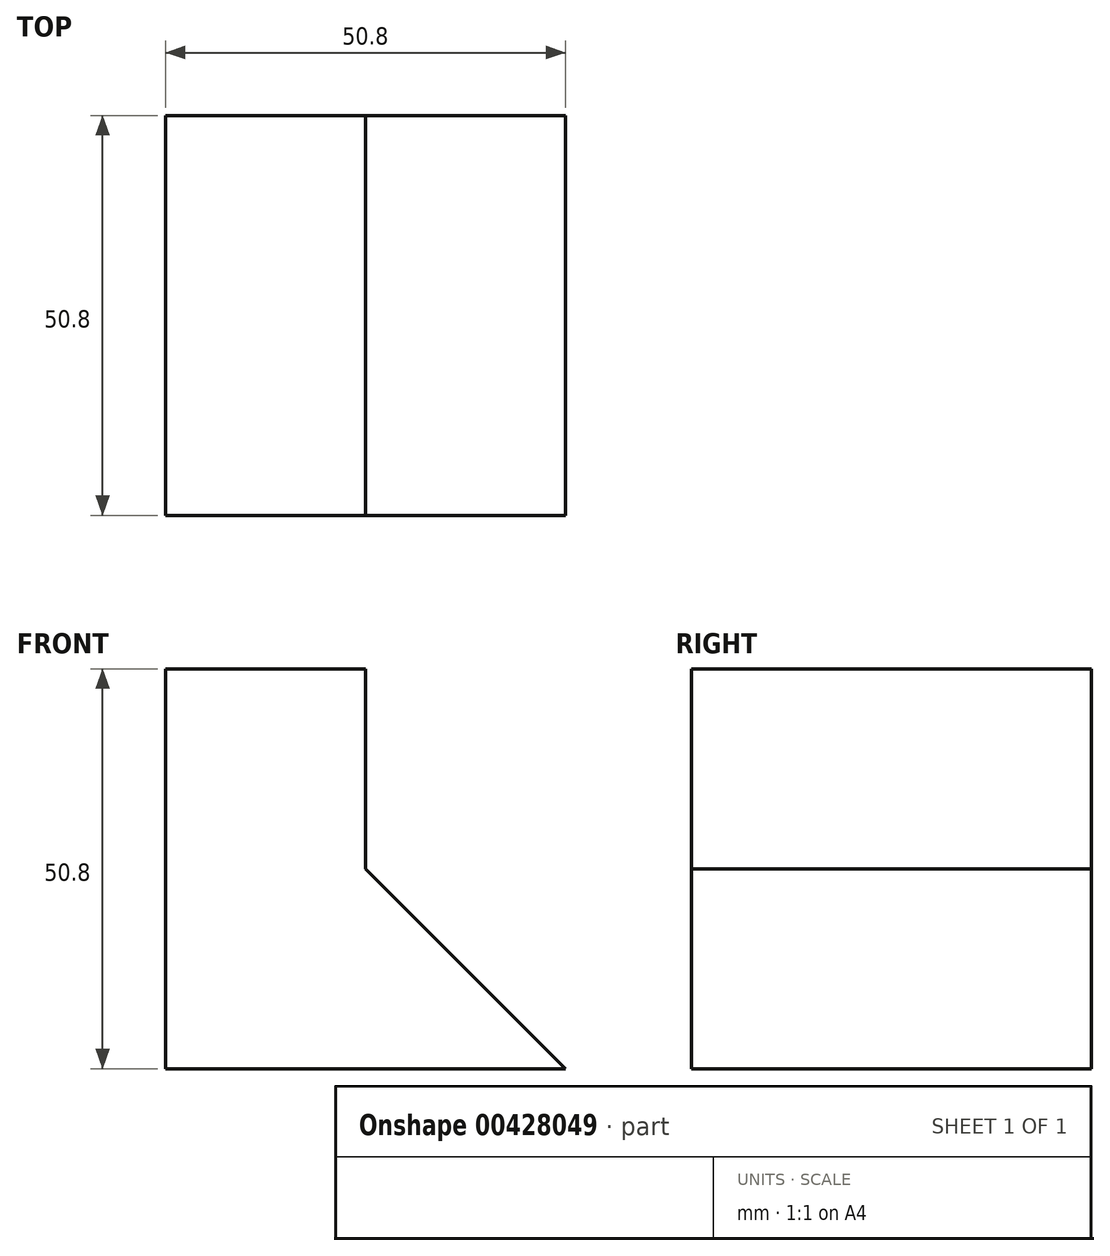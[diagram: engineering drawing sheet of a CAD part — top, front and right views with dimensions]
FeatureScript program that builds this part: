
annotation { "Feature Type Name" : "Feature", "Feature Type Description" : "" }
export const myFeature = defineFeature(function(context is Context, id is Id, definition is map)
    precondition{}
    {
        {
            var Q0;
            Q0=qCreatedBy(makeId("Front.planeOp"),FACE);
            var sketch = newSketch(context, id + "F0", { "sketchPlane" : qUnion([Q0])});
            skLineSegment(sketch, "E0", {"start": v(0, 0) * mm, "end": v(50.8, 0) * mm});
            skLineSegment(sketch, "E1", {"start": v(0, 0) * mm, "end": v(0, 50.8) * mm});
            skLineSegment(sketch, "E2", {"start": v(0, 50.8) * mm, "end": v(25.4, 50.8) * mm});
            skLineSegment(sketch, "E3", {"start": v(25.4, 50.8) * mm, "end": v(25.4, 25.4) * mm});
            skLineSegment(sketch, "E4", {"start": v(25.4, 25.4) * mm, "end": v(50.8, 0) * mm});
            skSolve(sketch);
        }
        {
            var Q0;
            Q0=makeQuery(id+"F0.imprint","IMPRINT",FACE,{"disambiguationData":[TD([[makeQuery(id+"F0.imprint","IMPRINT",EDGE,{"derivedFrom":sQuery(id+"F0.wireOp",EDGE,"E0")}),1.0]])]});
            extrude(context, id + "F1", {"entities" : qUnion([Q0]), "depth" : 50.8 * mm});
        }
    });
